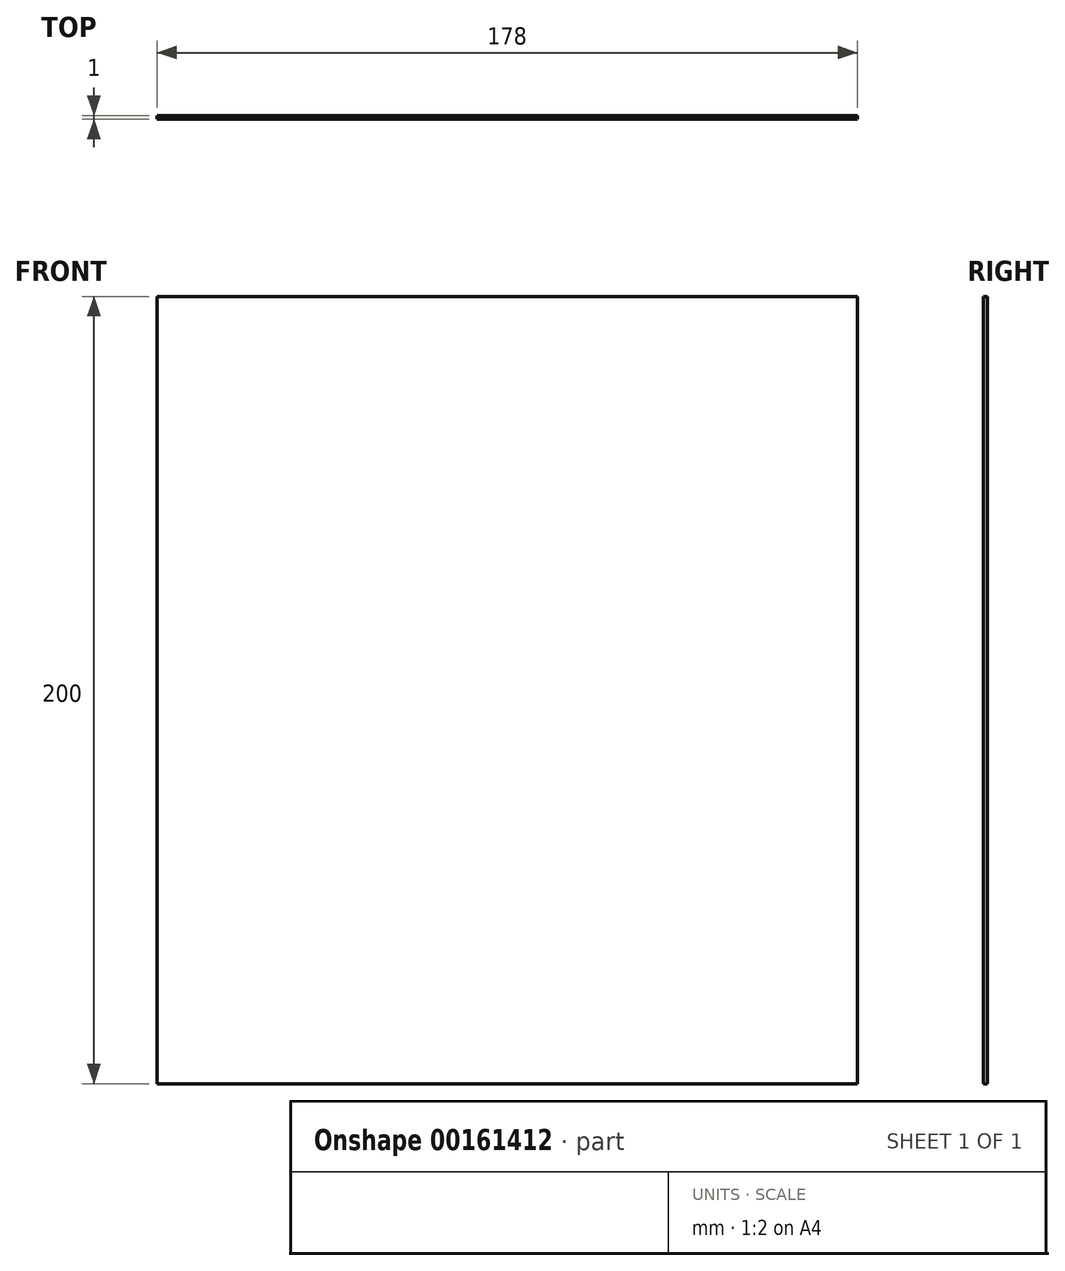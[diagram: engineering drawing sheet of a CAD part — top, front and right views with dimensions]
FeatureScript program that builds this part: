
annotation { "Feature Type Name" : "Feature", "Feature Type Description" : "" }
export const myFeature = defineFeature(function(context is Context, id is Id, definition is map)
    precondition{}
    {
        {
            var Q0;
            Q0=qCreatedBy(makeId("Front.planeOp"),FACE);
            var sketch = newSketch(context, id + "F0", { "sketchPlane" : qUnion([Q0])});
            skLineSegment(sketch, "E0.bottom", {"start": v(89, 95.92) * mm, "end": v(78.5, 95.92) * mm});
            skLineSegment(sketch, "E0.top", {"start": v(89, -104.08) * mm, "end": v(-89, -104.08) * mm});
            skLineSegment(sketch, "E0.left", {"start": v(89, 95.92) * mm, "end": v(89, -104.08) * mm});
            skLineSegment(sketch, "E0.right", {"start": v(-89, 75.92) * mm, "end": v(-89, -104.08) * mm});
            skPoint(sketch, "E0.middle", {"position": v(0, -4.08) * mm});
            skLineSegment(sketch, "E1.trimOffspring", {"start": v(22, 95.92) * mm, "end": v(-86, 95.92) * mm});
            skLineSegment(sketch, "E2", {"start": v(22, 95.92) * mm, "end": v(78.5, 95.92) * mm});
            skPoint(sketch, "E3.orphan", {"position": v(-89, 95.92) * mm});
            skLineSegment(sketch, "E4", {"start": v(-89, 95.92) * mm, "end": v(-89, 75.92) * mm});
            skLineSegment(sketch, "E5", {"start": v(-86, 95.92) * mm, "end": v(-89, 95.92) * mm});
            skSolve(sketch);
        }
        {
            var Q0;
            Q0=qSketchRegion(id+"F0",true);
            extrude(context, id + "F1", {"entities" : qUnion([Q0]), "depth" : 1 * mm});
        }
    });
